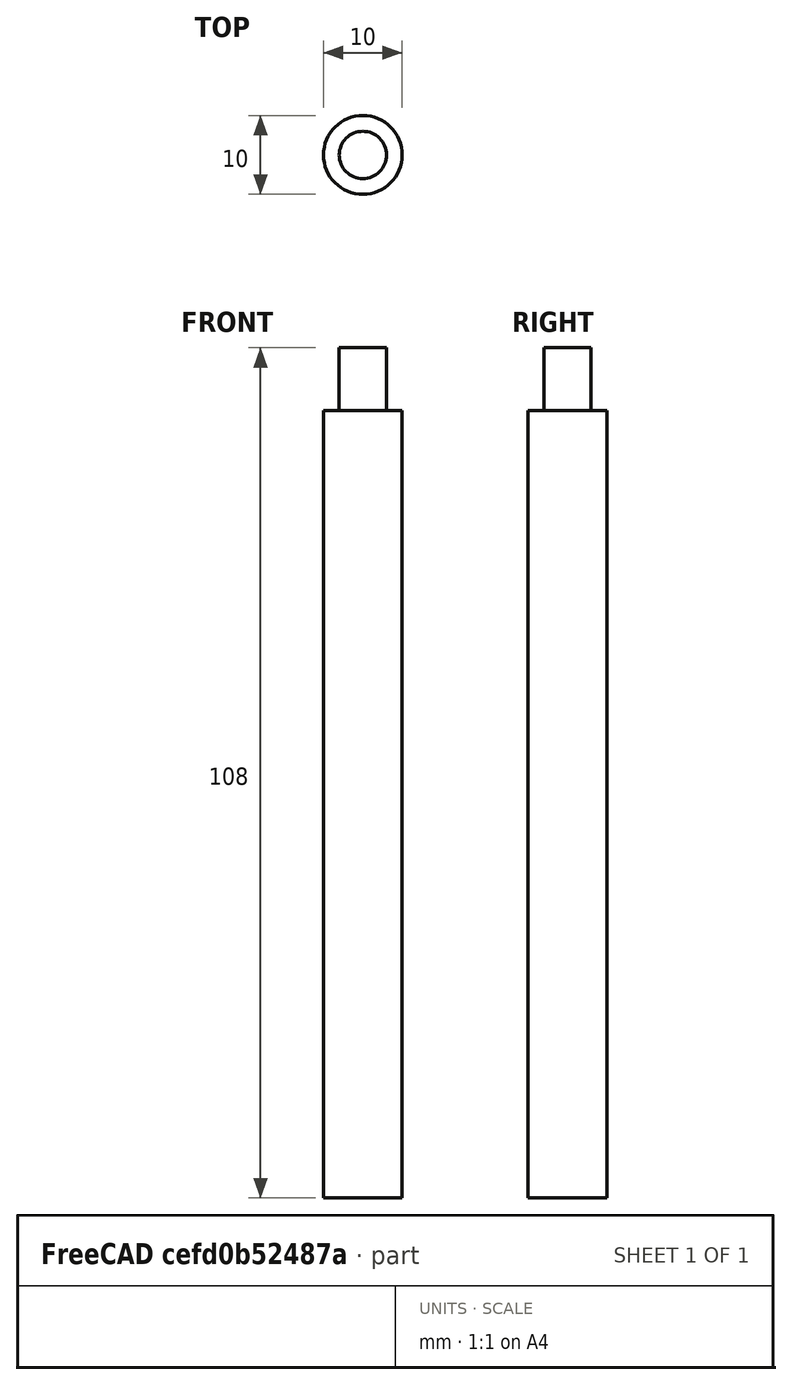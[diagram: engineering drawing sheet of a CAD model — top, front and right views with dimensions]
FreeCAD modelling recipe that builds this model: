
FCSTD DOCUMENT  (FreeCAD 0.18.4R)
Label: rod
Comment: # 2020-02-12 13:39:03: read from <userpath>/repositories/sussex_neuro/Olfactometer/hardware/mechanics/from_raiser_et_al/rod.ipt
License: All rights reserved
LicenseURL: http://en.wikipedia.org/wiki/All_rights_reserved
objects: Sketcher::SketchObject×4, Part::Extrusion×2, Spreadsheet::Sheet×1, Part::Feature×1
note: 7 computed .brp shape members not serialized (recipe doc carries the construction recipe); baked Part::Feature solids carry a one-line shape summary decoded from their .brp

FEATURE [Spreadsheet::Sheet] Parameters
  cells = A1=Parameter; B1=Value; C1=Fromula; D1=Tolerance; E1=Comment; A2=d0; B2(d0_)=10; C2=10mm; D2=NOMINAL; A3=d1; B3(d1_)=100; C3=100mm; D3=NOMINAL; A4=d10; B4(d10_)=45; C4=45°; D4=NOMINAL; A5=d2; B5(d2_)=0; C5=0°; D5=NOMINAL; A6=d3; B6(d3_)=6.000000000000001; C6=6mm; D6=NOMINAL; A7=d4; B7(d4_)=8; C7=8mm; D7=NOMINAL; A8=d5; B8(d5_)=0; C8=0°; D8=NOMINAL; A9=d6; B9(d6_)=10; C9=10mm; D9=NOMINAL; A10=d7; B10(d7_)=0; C10=0mm; D10=NOMINAL; A11=d8; B11(d8_)=1; C11=1mm; D11=NOMINAL; A12=d9; B12(d9_)=2; C12=2mm; D12=NOMINAL
FEATURE [Sketcher::SketchObject] Sketch1
  sketch-geometry (1):
    g0: Circle CenterX=0 CenterY=0 CenterZ=0 NormalX=0 NormalY=0 NormalZ=1 AngleXU=0 Radius=5
  constraints (1):
    c: Radius(g0) = 5  'd0'
FEATURE [Sketcher::SketchObject] Sketch1_bp
  sketch-geometry (1):
    g0: Circle CenterX=0 CenterY=0 CenterZ=0 NormalX=0 NormalY=0 NormalZ=1 AngleXU=0 Radius=5
FEATURE [Part::Extrusion] Extrusion1
  Base = -> Sketch1_bp
  Dir = (0,0,1)
  DirMode = 0
  FaceMakerClass = Part::FaceMakerBullseye
  LengthFwd = 100
  LengthRev = 0
  Solid = true
  Symmetric = false
  expr: LengthFwd = Parameters.d1_
  expr: TaperAngle = Parameters.d2_
FEATURE [Sketcher::SketchObject] Sketch3
  Placement = pos=(0,0,100) rot=(0,0,1;0rad)
  sketch-geometry (2):
    g0: Circle [constr] CenterX=0 CenterY=0 CenterZ=0 NormalX=0 NormalY=0 NormalZ=1 AngleXU=0 Radius=5
    g1: Circle CenterX=0 CenterY=0 CenterZ=0 NormalX=0 NormalY=0 NormalZ=1 AngleXU=0 Radius=3
  constraints (1):
    c: Radius(g1) = 3  'd3'
FEATURE [Sketcher::SketchObject] Sketch3_bp
  Placement = pos=(0,0,100) rot=(0,0,1;0rad)
  sketch-geometry (1):
    g0: Circle CenterX=0 CenterY=0 CenterZ=0 NormalX=0 NormalY=0 NormalZ=1 AngleXU=0 Radius=3
FEATURE [Part::Extrusion] Extrusion2
  Base = -> Sketch3_bp
  Dir = (0,0,1)
  DirMode = 0
  FaceMakerClass = Part::FaceMakerBullseye
  LengthFwd = 8
  LengthRev = 0
  Solid = true
  Symmetric = false
  expr: LengthFwd = Parameters.d4_
  expr: TaperAngle = Parameters.d5_
FEATURE [Part::Feature] Thread1
  shape: bbox 6 x 6 x 8 mm, 2 faces, 0 solids (baked)
